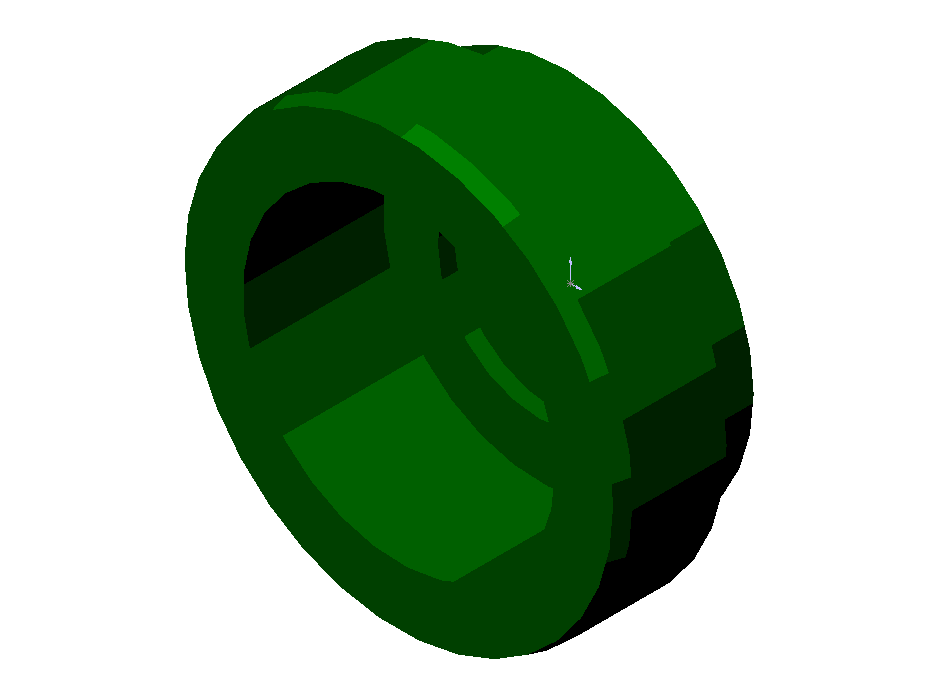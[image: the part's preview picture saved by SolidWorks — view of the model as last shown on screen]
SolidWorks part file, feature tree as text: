
SOLIDWORKS PART (.sldprt)
format: sldprt  version: not decoded by parser v0  size: 104,960 bytes
history: native  units: mm
features: sketch x5, plane x3, cut_extrude x3, extrude x2, material x1, chamfer x1 (+10 scaffold rows collapsed)
feature tree (25):
  scaffold x10  (default folders/planes/origin — collapsed)
  material  "Matériau <non spécifié>"
  plane  "Plan1"
  plane  "Plan2"
  plane  "Plan3"
  sketch  "Esquisse1"  dims[D1=12.0mm]
  extrude  "Base-Extrusion"  Depth=2mm
  sketch  "Esquisse2"  dims[D1=14.0mm]
  extrude  "Boss.-Extru.1"  Depth=3.5mm
  sketch  "Esquisse3"  dims[D1=10.0mm]
  cut_extrude  "Enlèv. mat.-Extru.1"  Depth=4mm
  sketch  "Esquisse4"  dims[D1=6.5mm]
  cut_extrude  "Enlèv. mat.-Extru.2"  Depth=0.5mm
  sketch  "Esquisse5"  dims[D1=4.2mm]
  cut_extrude  "Enlèv. mat.-Extru.3"  [1 undecoded]
  chamfer  "Chanfrein1"  Distance=0.5mm Angle=15deg
decode coverage: 10 of 11 modeling features carry decoded parameters
note: 1 parameter value undecoded
note: suppression state not decoded; provenance and decode notes live in map.json
